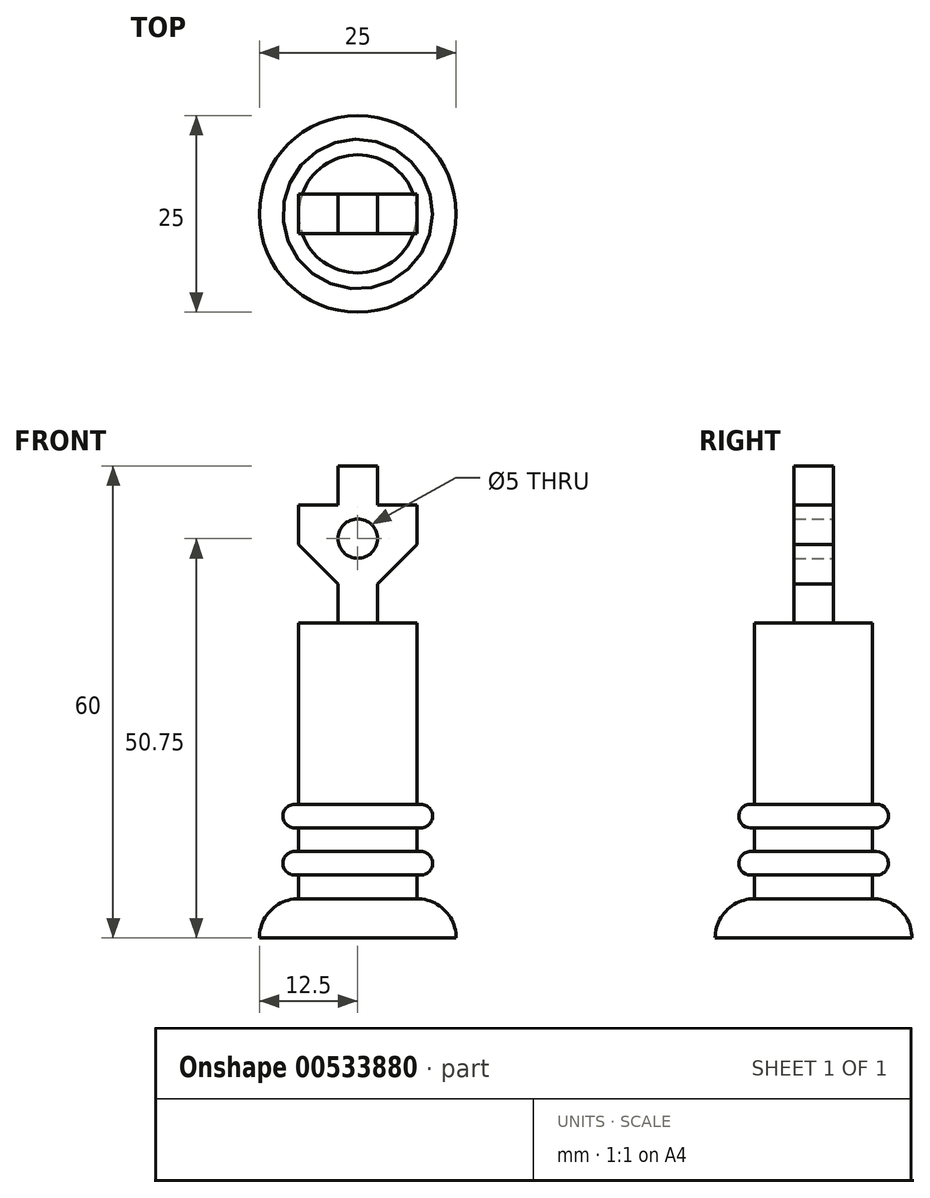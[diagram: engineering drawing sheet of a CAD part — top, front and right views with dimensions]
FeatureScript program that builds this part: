
annotation { "Feature Type Name" : "Feature", "Feature Type Description" : "" }
export const myFeature = defineFeature(function(context is Context, id is Id, definition is map)
    precondition{}
    {
        {
            assignVariable(context, id + "F0", {"name" : "base_height", "anyValue" : 5});
        }
        {
            assignVariable(context, id + "F1", {"name" : "tower_height", "anyValue" : 40});
        }
        {
            assignVariable(context, id + "F2", {"name" : "ring_height", "anyValue" : 3});
        }
        {
            var Q0;
            Q0=qCreatedBy(makeId("Top.planeOp"),FACE);
            var sketch = newSketch(context, id + "F3", { "sketchPlane" : qUnion([Q0])});
            skCircle(sketch, "E0", {"center": v(0, 0) * mm, "radius": 12.5 * mm});
            skCircle(sketch, "E1", {"center": v(0, 0) * mm, "radius": 7.5 * mm});
            skCircle(sketch, "E2.0", {"center": v(0, 0) * mm, "radius": 9.5 * mm});
            skSolve(sketch);
        }
        {
            var Q0;
            Q0=makeQuery(id+"F3.imprint","IMPRINT",FACE,{"disambiguationData":[TD([[makeQuery(id+"F3.imprint","IMPRINT",EDGE,{"derivedFrom":sQuery(id+"F3.wireOp",EDGE,"E0")}),1.0]])]});
            var Q1;
            Q1=makeQuery(id+"F3.imprint","IMPRINT",FACE,{"disambiguationData":[TD([[makeQuery(id+"F3.imprint","IMPRINT",EDGE,{"derivedFrom":sQuery(id+"F3.wireOp",EDGE,"E1")}),-1.0]])]});
            var Q2;
            Q2=makeQuery(id+"F3.imprint","IMPRINT",FACE,{"disambiguationData":[TD([[makeQuery(id+"F3.imprint","IMPRINT",EDGE,{"derivedFrom":sQuery(id+"F3.wireOp",EDGE,"E1")}),1.0]])]});
            extrude(context, id + "F4", {"entities" : qUnion([Q0, Q1, Q2]), "depth" : getVariable(context, 'base_height') * mm, "offsetDistance" : 25 * mm});
        }
        {
            var Q0;
            Q0=makeQuery(id+"F3.imprint","IMPRINT",FACE,{"disambiguationData":[TD([[makeQuery(id+"F3.imprint","IMPRINT",EDGE,{"derivedFrom":sQuery(id+"F3.wireOp",EDGE,"E1")}),1.0]])]});
            extrude(context, id + "F5", {"entities" : qUnion([Q0]), "operationType" : NewBodyOperationType.ADD, "depth" : (getVariable(context, 'tower_height')) * mm, "offsetDistance" : 25 * mm});
        }
        {
            var Q0;
            Q0=makeQuery(id+"F3.imprint","IMPRINT",FACE,{"disambiguationData":[TD([[makeQuery(id+"F3.imprint","IMPRINT",EDGE,{"derivedFrom":sQuery(id+"F3.wireOp",EDGE,"E1")}),-1.0]])]});
            extrude(context, id + "F6", {"entities" : qUnion([Q0]), "operationType" : NewBodyOperationType.ADD, "depth" : (getVariable(context, 'base_height') + getVariable(context, 'ring_height') * 2) * mm, "offsetDistance" : 25 * mm, "hasSecondDirection" : true, "secondDirectionOppositeDirection" : false, "secondDirectionDepth" : (getVariable(context, 'base_height') + getVariable(context, 'ring_height')) * mm});
        }
        {
            var Q0;
            Q0=makeQuery(id+"F3.imprint","IMPRINT",FACE,{"disambiguationData":[TD([[makeQuery(id+"F3.imprint","IMPRINT",EDGE,{"derivedFrom":sQuery(id+"F3.wireOp",EDGE,"E1")}),-1.0]])]});
            extrude(context, id + "F7", {"entities" : qUnion([Q0]), "operationType" : NewBodyOperationType.ADD, "depth" : (getVariable(context, 'base_height') + getVariable(context, 'ring_height') * 4) * mm, "offsetDistance" : 25 * mm, "hasSecondDirection" : true, "secondDirectionOppositeDirection" : false, "secondDirectionDepth" : (getVariable(context, 'base_height') + getVariable(context, 'ring_height') * 3) * mm});
        }
        {
            var Q0;
            Q0=makeQuery(id+"F6.opExtrude","CAP_EDGE",EDGE,{"disambiguationData":[OSD([sQuery(id+"F3.wireOp",EDGE,"E2.0")])],"isStart":true});
            var Q1;
            Q1=makeQuery(id+"F6.opExtrude","CAP_EDGE",EDGE,{"disambiguationData":[OSD([sQuery(id+"F3.wireOp",EDGE,"E2.0")])],"isStart":false});
            fillet(context, id + "F8", {"entities" : qUnion([Q0, Q1]), "radius" : 1.5 * mm, "tangentPropagation" : true, "allowEdgeOverflow" : false});
        }
        {
            var Q0;
            Q0=makeQuery(id+"F7.opExtrude","CAP_EDGE",EDGE,{"disambiguationData":[OSD([sQuery(id+"F3.wireOp",EDGE,"E2.0")])],"isStart":true});
            var Q1;
            Q1=makeQuery(id+"F7.opExtrude","CAP_EDGE",EDGE,{"disambiguationData":[OSD([sQuery(id+"F3.wireOp",EDGE,"E2.0")])],"isStart":false});
            fillet(context, id + "F9", {"entities" : qUnion([Q0, Q1]), "radius" : 1.5 * mm, "tangentPropagation" : true, "allowEdgeOverflow" : false});
        }
        {
            var Q0;
            Q0=makeQuery(id+"F4.opExtrude","CAP_EDGE",EDGE,{"disambiguationData":[OSD([sQuery(id+"F3.wireOp",EDGE,"E0")])],"isStart":false});
            fillet(context, id + "F10", {"entities" : qUnion([Q0]), "radius" : (getVariable(context, 'base_height')) * mm, "tangentPropagation" : true, "allowEdgeOverflow" : false});
        }
        {
            assignVariable(context, id + "F11", {"name" : "tip_depth", "anyValue" : 5});
        }
        {
            assignVariable(context, id + "F12", {"name" : "tip_base_width", "anyValue" : 5});
        }
        {
            assignVariable(context, id + "F13", {"name" : "crown_width", "anyValue" : 15});
        }
        {
            var Q0;
            Q0=qCreatedBy(makeId("Front.planeOp"),FACE);
            var sketch = newSketch(context, id + "F14", { "sketchPlane" : qUnion([Q0])});
            skLineSegment(sketch, "E3", {"start": v(0, 0) * mm, "end": v(0, 40) * mm, "construction": true});
            skLineSegment(sketch, "E4", {"start": v(-2.5, 40) * mm, "end": v(2.5, 40) * mm});
            skLineSegment(sketch, "E5", {"start": v(-2.5, 40) * mm, "end": v(-2.5, 50) * mm});
            skLineSegment(sketch, "E6", {"start": v(2.5, 40) * mm, "end": v(2.5, 50) * mm});
            skLineSegment(sketch, "E7", {"start": v(2.5, 50) * mm, "end": v(7.5, 50) * mm});
            skLineSegment(sketch, "E8", {"start": v(-2.5, 50) * mm, "end": v(-7.5, 50) * mm});
            skLineSegment(sketch, "E9", {"start": v(7.5, 50) * mm, "end": v(7.5, 55) * mm});
            skLineSegment(sketch, "E10", {"start": v(-7.5, 50) * mm, "end": v(-7.5, 55) * mm});
            skLineSegment(sketch, "E11", {"start": v(7.5, 55) * mm, "end": v(2.5, 55) * mm});
            skLineSegment(sketch, "E12", {"start": v(-7.5, 55) * mm, "end": v(-2.5, 55) * mm});
            skLineSegment(sketch, "E13", {"start": v(2.5, 55) * mm, "end": v(2.5, 60) * mm});
            skLineSegment(sketch, "E14", {"start": v(-2.5, 55) * mm, "end": v(-2.5, 60) * mm});
            skLineSegment(sketch, "E15", {"start": v(-2.5, 60) * mm, "end": v(2.5, 60) * mm});
            skLineSegment(sketch, "E16", {"start": v(0, 40) * mm, "end": v(0, 50.75) * mm, "construction": true});
            skCircle(sketch, "E17", {"center": v(0, 50.75) * mm, "radius": 2.5 * mm});
            skSolve(sketch);
        }
        {
            var Q0;
            Q0=makeQuery(id+"F14.imprint","IMPRINT",FACE,{"disambiguationData":[TD([[makeQuery(id+"F14.imprint","IMPRINT",EDGE,{"derivedFrom":sQuery(id+"F14.wireOp",EDGE,"E4")}),1.0]])]});
            extrude(context, id + "F15", {"entities" : qUnion([Q0]), "operationType" : NewBodyOperationType.ADD, "depth" : (getVariable(context, 'tip_depth') / 2) * mm, "offsetDistance" : 25 * mm, "hasSecondDirection" : true, "secondDirectionOppositeDirection" : true, "secondDirectionDepth" : (getVariable(context, 'tip_depth') / 2) * mm});
        }
        {
            var Q0;
            Q0=makeQuery(id+"F15.opExtrude","SWEPT_EDGE",EDGE,{"disambiguationData":[OSD([sQuery(id+"F14.wireOp",EDGE,"E5"),sQuery(id+"F14.wireOp",EDGE,"E8")])]});
            var Q1;
            Q1=makeQuery(id+"F15.opExtrude","SWEPT_EDGE",EDGE,{"disambiguationData":[OSD([sQuery(id+"F14.wireOp",EDGE,"E6"),sQuery(id+"F14.wireOp",EDGE,"E7")])]});
            chamfer(context, id + "F16", {"entities" : qUnion([Q0, Q1]), "width" : ((getVariable(context, 'crown_width') - getVariable(context, 'tip_base_width')) / 2) * mm, "tangentPropagation" : true});
        }
    });
